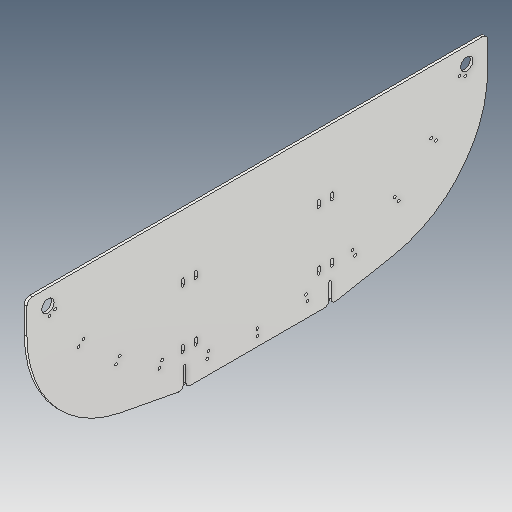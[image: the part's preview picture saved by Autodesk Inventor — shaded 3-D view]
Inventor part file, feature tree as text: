
AUTODESK INVENTOR PART (.ipt)
format: ipt  version: 2023.5 (Build 275446000, 446)  size: 153,600 bytes
history: native  units: in
note: dims shown in document units (in); Inventor stores cm internally (conversion verified against a paired STEP export)
features: fillet x1
ambient origin geometry x8: Origin, YZ Plane, XZ Plane, XY Plane, X Axis, Y Axis, Z Axis, Center Point
bodies: Solid1 (feature_tree)
feature tree (1):
  fillet  "Fillet4"  [1 undecoded]
note: 1 required parameter value undecoded (feature->parameter linkage not recoverable at this tier; creation-order binding heuristic only, values carry confidence <= 0.55)
